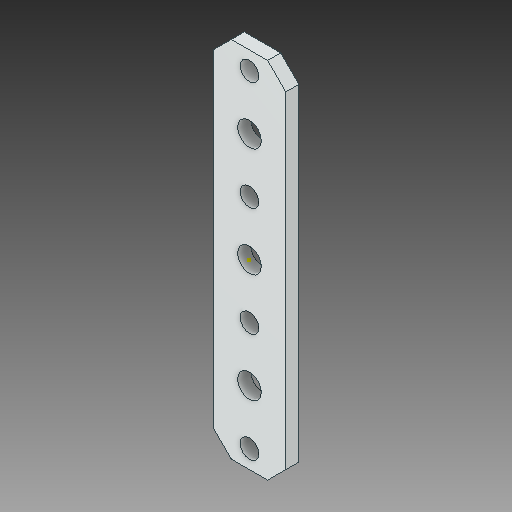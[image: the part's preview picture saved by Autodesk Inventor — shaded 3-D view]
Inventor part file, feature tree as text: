
AUTODESK INVENTOR PART (.ipt)
format: ipt  version: 2017 (Build 210142000, 142)  size: 113,152 bytes
history: native  units: in
note: dims shown in document units (in); Inventor stores cm internally (conversion verified against a paired STEP export)
features: sketch x1, other x1
ambient origin geometry x8: Origin, YZ Plane, XZ Plane, XY Plane, X Axis, Y Axis, Z Axis, Center Point
bodies: Solid1 (feature_tree)
feature tree (2):
  sketch  "Sketch1"
  other  "Break-Corner1"
